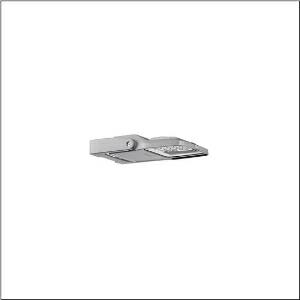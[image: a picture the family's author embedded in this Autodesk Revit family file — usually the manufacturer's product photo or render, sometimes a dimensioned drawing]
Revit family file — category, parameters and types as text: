
# Revit family: floodlight_fl_21_iq_micro___pl33t_5xa7762a4f2a_0497
name_source: partatom
category: Lighting Fixtures
units: mm (PartAtom-declared; Revit-internal decimal feet)

## family parameters
Cut with Voids When Loaded = No
Host = Face
Light Source = No
Part Type = Normal
Room Calculation Point = No
Round Connector Dimension = Use Diameter
Shared = No

## types (1)
- --- (1 x LED, 3050 lm, 23.1 W, 4000K)
    Apparent Load = 23 VA
    CIE Flux Codes = 26 75 99 100 100
    Color Rendering = 70
    Color Temperature = 4000K
    Default Elevation = 1800 mm
    Description = Floodlight FL 21 iQ micro, floodlight, primary light control with lens, of PMMA, primary optical cover: protective disc, of toughened safety glass, transparent, light distribution: PL33T, light emission: direct distribution, installation type: surface-mounted, LED, High Power LED, rated luminous flux: 3.050lm, luminous efficacy: 132lm/W, light colour: 740, colour temperature: 4000K, control gear: iQ Street-Remote/DALI, control: Auto-Match, Temp-Guard, Night-Set, Smart-Wire, Desk-Remote (wireless, voltage-free reading and setting of iQ features in the workshop via application-optimized NFC function/RFID function), optimised constant luminous flux control (CLO 2.0), Street-Remote, with terminal, 6-pole, mains connection: 220..240V, AC, 50/60Hz, start of lifetime: 23W, end of service life: 24W, reduction: 11W, luminaire housing, of diecast aluminium, powder-coated, Siteco® metallic grey (DB 702S), corrosivity category C5 mid according to DIN EN ISO 12944, suitable for swimming pools, chlorine-resistant, sealing non-destructively replaceable, design bracket, of diecast aluminium, powder-coated, Siteco® metallic grey (DB 702S), protection rating (complete): IP66, insulation class (complete): insulation class II (safety insulation), certification: CE, ENEC, VDE, protection symbol: D, impact resistance: IK07, permissible operating ambient temperature: -40..+40°C, permissible operating ambient temperature for outdoor applications: -40..+50°C, standard: DIN EN 12944, LABS conformity tested according to VDMA 24364:2018-05, packaging unit: 1 piece

Light Distribution: PL33T
    Height = 65 mm
    Lamp = 1 x LED
    Lamp Light Flux = 3050 lm
    Lamp Power = 23.1 W
    Lamp count = 1
    Length = 312 mm
    Luminous efficacy = 132 lm/W
    Manufacturer = Siteco
    ModVariant = No
    Model = 5XA7762A4F2A
    Mounting Place = Wall
    Mounting Type = Surface mounted
    Number of Poles = 1
    OnlyDefault = Yes
    Power Factor = 1
    Product Name = Floodlight FL 21 iQ micro | PL33T
    Product group = floodlight | wall mounted
    ProductGroupID = 2001
    Protection Class = Protection class II
    Protection Degree = IP 66
    RLX_Detail_Level = 1
    RLX_Emergency_Light_Flux = 0 lm
    RLX_Emergency_Type = 0
    RLX_Emergency_Type_DB = No
    RlxData = <blob elided: 97513 chars, md5=6a4c518d>
    Socket = socket
    Standby Power = 0 W
    System Light Flux = 3050 lm
    System Power = 23 W
    Type Comments = factory setting: luminous flux: 100 % | dim-lin: 254 | 455 mA
    Type Image = l_1006878.jpg
    URL = http://relux.com
    VarID = @adj_147902
    Voltage = 0 V
    Weight = 0.00 kg
    Width = 230 mm

## geometry (parser evidence)
native form markers: Blend x4, Sweep x13
no freeform markers — native parametric forms only
